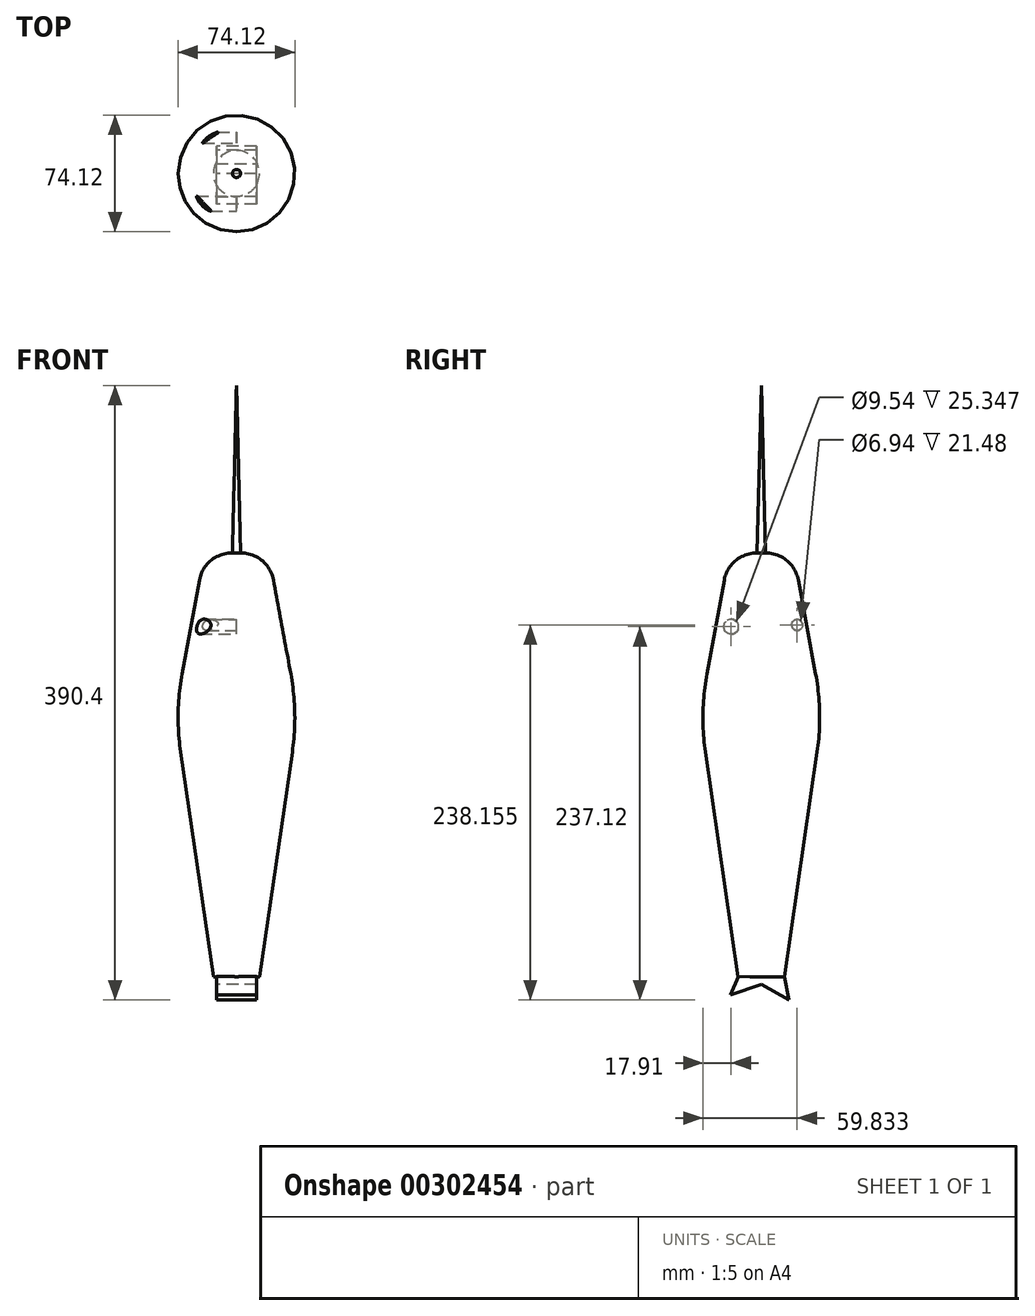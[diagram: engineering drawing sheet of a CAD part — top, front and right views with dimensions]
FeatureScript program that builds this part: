
annotation { "Feature Type Name" : "Feature", "Feature Type Description" : "" }
export const myFeature = defineFeature(function(context is Context, id is Id, definition is map)
    precondition{}
    {
        {
            var Q0;
            Q0=qCreatedBy(makeId("Top.planeOp"),FACE);
            cPlane(context, id + "F0", {"entities" : qUnion([Q0]), "cplaneType" : CPlaneType.OFFSET, "offset" : 101.6 * mm, "width" : 152.4 * mm, "height" : 152.4 * mm});
        }
        {
            var Q0;
            Q0=qCreatedBy(makeId("Top.planeOp"),FACE);
            var sketch = newSketch(context, id + "F1", { "sketchPlane" : qUnion([Q0])});
            skCircle(sketch, "E0", {"center": v(0, 0) * mm, "radius": 39.1 * mm});
            skSolve(sketch);
        }
        {
            var Q0;
            Q0=qCreatedBy(id+"F0.planeOp",FACE);
            var sketch = newSketch(context, id + "F2", { "sketchPlane" : qUnion([Q0])});
            skCircle(sketch, "E1", {"center": v(0, 0) * mm, "radius": 20.32 * mm});
            skSolve(sketch);
        }
        {
            var Q0;
            Q0=makeQuery(id+"F2.imprint","IMPRINT",FACE,{"disambiguationData":[TD([[makeQuery(id+"F2.imprint","IMPRINT",EDGE,{"derivedFrom":sQuery(id+"F2.wireOp",EDGE,"E1")}),1.0]])]});
            var Q1;
            Q1=makeQuery(id+"F1.imprint","IMPRINT",FACE,{"disambiguationData":[TD([[makeQuery(id+"F1.imprint","IMPRINT",EDGE,{"derivedFrom":sQuery(id+"F1.wireOp",EDGE,"E0")}),1.0]])]});
            loft(context, id + "F3", {"sheetProfilesArray" : [{ "sheetProfileEntities" : qUnion([Q0]) }, { "sheetProfileEntities" : qUnion([Q1]) }]});
        }
        {
            var Q0;
            Q0=makeQuery(id+"F3.opLoft","CAP_FACE",FACE,{"disambiguationData":[OSD([makeQuery(id+"F2.imprint","IMPRINT",FACE,{"disambiguationData":[TD([[makeQuery(id+"F2.imprint","IMPRINT",EDGE,{"derivedFrom":sQuery(id+"F2.wireOp",EDGE,"E1")}),1.0]])]})])],"isStart":true});
            fillet(context, id + "F4", {"entities" : qUnion([Q0]), "radius" : 21.1 * mm, "tangentPropagation" : true, "allowEdgeOverflow" : false});
        }
        {
            var Q0;
            Q0=qCreatedBy(id+"F0.planeOp",FACE);
            var sketch = newSketch(context, id + "F5", { "sketchPlane" : qUnion([Q0])});
            skCircle(sketch, "E2", {"center": v(0, 0) * mm, "radius": 2.58 * mm});
            skSolve(sketch);
        }
        {
            var Q0;
            Q0=qCreatedBy(id+"F0.planeOp",FACE);
            cPlane(context, id + "F6", {"entities" : qUnion([Q0]), "cplaneType" : CPlaneType.OFFSET, "offset" : 106.43 * mm, "width" : 152.4 * mm, "height" : 152.4 * mm});
        }
        {
            var Q0;
            Q0=qCreatedBy(id+"F6.planeOp",FACE);
            var sketch = newSketch(context, id + "F7", { "sketchPlane" : qUnion([Q0])});
            skCircle(sketch, "E3", {"center": v(0, 0) * mm, "radius": 1.25 * mm});
            skSolve(sketch);
        }
        {
            var Q1;
            Q1=makeQuery(id+"F5.imprint","IMPRINT",FACE,{"disambiguationData":[TD([[makeQuery(id+"F5.imprint","IMPRINT",EDGE,{"derivedFrom":sQuery(id+"F5.wireOp",EDGE,"E2")}),1.0]])]});
            var Q2;
            Q2=sQuery(id+"F7.wireOp",VERTEX,"E3.center");
            loft(context, id + "F8", {"operationType" : NewBodyOperationType.ADD, "sheetProfilesArray" : [{ "sheetProfileEntities" : qUnion([Q1]) }, { "sheetProfileEntities" : qUnion([Q2]) }]});
        }
        {
            var Q0;
            Q0=qCreatedBy(makeId("Top.planeOp"),FACE);
            cPlane(context, id + "F9", {"entities" : qUnion([Q0]), "cplaneType" : CPlaneType.OFFSET, "offset" : 167.64 * mm, "oppositeDirection" : true, "width" : 152.4 * mm, "height" : 152.4 * mm});
        }
        {
            var Q0;
            Q0=qCreatedBy(id+"F9.planeOp",FACE);
            var sketch = newSketch(context, id + "F10", { "sketchPlane" : qUnion([Q0])});
            skCircle(sketch, "E4", {"center": v(0, 0) * mm, "radius": 14.65 * mm});
            skSolve(sketch);
        }
        {
            var Q1;
            Q1=makeQuery(id+"F3.opLoft","CAP_FACE",FACE,{"disambiguationData":[OSD([makeQuery(id+"F1.imprint","IMPRINT",FACE,{"disambiguationData":[TD([[makeQuery(id+"F1.imprint","IMPRINT",EDGE,{"derivedFrom":sQuery(id+"F1.wireOp",EDGE,"E0")}),1.0]])]})])],"isStart":true});
            var Q2;
            Q2=makeQuery(id+"F10.imprint","IMPRINT",FACE,{"disambiguationData":[TD([[makeQuery(id+"F10.imprint","IMPRINT",EDGE,{"derivedFrom":sQuery(id+"F10.wireOp",EDGE,"E4")}),1.0]])]});
            loft(context, id + "F11", {"operationType" : NewBodyOperationType.ADD, "sheetProfilesArray" : [{ "sheetProfileEntities" : qUnion([Q1]) }, { "sheetProfileEntities" : qUnion([Q2]) }]});
        }
        {
            var Q0;
            {var subQ0=sQuery(id+"F2.wireOp",EDGE,"E1");var subQ1=sQuery(id+"F1.wireOp",EDGE,"E0");Q0=makeQuery(id+"F11.boolean.opBoolean","MERGE",EDGE,{"derivedFrom":[makeQuery(id+"F3.opLoft","MID_CAP_EDGE",EDGE,{"disambiguationData":[OSD([subQ1,subQ0])],"capPos":1.0}),makeQuery(id+"F11.opLoft","MID_CAP_EDGE",EDGE,{"disambiguationData":[OSD([subQ1,subQ0])],"capPos":0.0})]});}
            fillet(context, id + "F12", {"entities" : qUnion([Q0]), "radius" : 152.4 * mm, "tangentPropagation" : true, "allowEdgeOverflow" : false});
        }
        {
            var Q0;
            Q0=qCreatedBy(makeId("Right.planeOp"),FACE);
            var sketch = newSketch(context, id + "F13", { "sketchPlane" : qUnion([Q0])});
            skLineSegment(sketch, "E5", {"start": v(-14.6, -167.56) * mm, "end": v(-19.4, -179.07) * mm});
            skLineSegment(sketch, "E6", {"start": v(-19.4, -179.07) * mm, "end": v(0, -172.46) * mm});
            skLineSegment(sketch, "E7", {"start": v(0, -172.46) * mm, "end": v(17.53, -182.37) * mm});
            skLineSegment(sketch, "E8", {"start": v(17.53, -182.37) * mm, "end": v(14.8, -167.67) * mm});
            skLineSegment(sketch, "E9", {"start": v(14.8, -167.67) * mm, "end": v(-14.6, -167.56) * mm});
            skSolve(sketch);
        }
        {
            var Q0;
            Q0=makeQuery(id+"F13.imprint","IMPRINT",FACE,{"disambiguationData":[TD([[makeQuery(id+"F13.imprint","IMPRINT",EDGE,{"derivedFrom":sQuery(id+"F13.wireOp",EDGE,"E5")}),1.0]])]});
            extrude(context, id + "F14", {"entities" : qUnion([Q0]), "operationType" : NewBodyOperationType.ADD, "depth" : 12.7 * mm});
        }
        {
            var Q0;
            Q0 = qSketchRegion(id + "F13", true);
            extrude(context, id + "F15", {"entities" : qUnion([Q0]), "operationType" : NewBodyOperationType.ADD, "oppositeDirection" : true, "depth" : 12.7 * mm});
        }
        {
            var Q0;
            Q0=qCreatedBy(makeId("Right.planeOp"),FACE);
            var sketch = newSketch(context, id + "F16", { "sketchPlane" : qUnion([Q0])});
            skCircle(sketch, "E10", {"center": v(22.77, 55.79) * mm, "radius": 3.47 * mm});
            skCircle(sketch, "E11", {"center": v(-19.15, 54.75) * mm, "radius": 4.77 * mm});
            skSolve(sketch);
        }
        {
            var Q0;
            Q0 = qSketchRegion(id + "F16", true);
            extrude(context, id + "F17", {"entities" : qUnion([Q0]), "operationType" : NewBodyOperationType.REMOVE, "oppositeDirection" : true, "depth" : 25.4 * mm});
        }
    });
